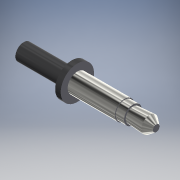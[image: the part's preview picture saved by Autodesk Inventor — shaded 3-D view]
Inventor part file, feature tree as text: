
AUTODESK INVENTOR PART (.ipt)
format: ipt  version: 2018 (Build 220112000, 112)  size: 135,680 bytes
history: native  units: mm
features: revolve x1, sketch x1
ambient origin geometry x8: Origin, YZ Plane, XZ Plane, XY Plane, X Axis, Y Axis, Z Axis, Center Point
bodies: Solid1 (feature_tree)
feature tree (2):
  revolve  "Revolution1"  [1 undecoded]
  sketch  "Sketch1"  dims[d1=1.0mm d3=14.0mm d5=6.0mm d6=3.5mm d7=3.2mm d8=2.6mm d9=3.0mm d11=14.0mm d12=11.0mm d13=9.5mm d15=1.2mm d16=1.2mm d17=8.652838mm d18=90.0deg]
note: 1 required parameter value undecoded (feature->parameter linkage not recoverable at this tier; creation-order binding heuristic only, values carry confidence <= 0.55)
